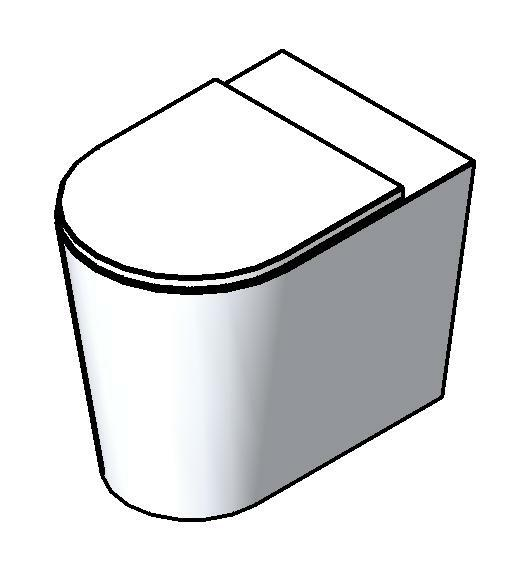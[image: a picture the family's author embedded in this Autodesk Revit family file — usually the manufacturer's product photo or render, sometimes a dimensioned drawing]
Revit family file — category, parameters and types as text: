
# Revit family: Deca_Bacia Sanitaria Convencional_LK_P.23
name_source: partatom
category: Plumbing Fixtures
units: mm (PartAtom-declared; Revit-internal decimal feet)

## family parameters
Cut with Voids When Loaded = No
Host = Face
Part Type = Normal
Room Calculation Point = No
Round Connector Dimension = Use Radius
Shared = No

## types (5) — shared parameters
Acompanha o Produto = -
Aprovado por = quattroD
Atendimento ao Cliente = 0800-0117073
Categoria = BACIAS E BIDES
Composição Anel Vedação = Não Possui
Composição Assento = -
Composição Básica = Argila, feldspato, caulim, vidrados e corantes inorgânicos.
Composição Componente = Não Possui
Consumo = 6 lpf
Cor Interna = -
Cor Secundária = -
Cores Componente = -
Criado por = quattroD
Código Pai = P.23
Description = Bacia convencional
Diâmetro Ponto de Esgoto = 0.1 m
Diâmetro Água Fria = 0.04 m
Informações Complementares = -
Itens de Instalação = 1200.C.KIT.P
Linha = LK
Manufacturer = Deca
Norma = NBR-16727-1;NBR-16727-2
Peso Líquido (Kg) = 32.341
Pressão máx. funcionamento = -
Pressão mín. Aquec. Acúmulo = -
Pressão mín. Aquec. Passagem = -
Pressão mín. funcionamento = -
Raio Ponto de Esgoto = 0.05 m
Raio Água Fria = 0.02 m
Saída de Esgoto = Saída de Esgoto Vertical
Segmento = Banheiro Luxo
Tipo de dispositivo economizador = -
Tipo de mecanismo utilizado = -
Tipo de rosca de entrada = -
Tipo de rosca de saída = -
URL = www.deca.com.br
Vazão na Pressão máx. (L/min) = -
Vazão na Pressão mín. (L/min) = -
zero-valued in all types: CWFU, Default Elevation, WFU

## per-type parameters (varying)
| type | Cor Principal | Material | Model |
| P.23.86_Cinza Fosco | Cinza Fosco | Deca_Cinza Fosco | P.23.86 |
| P.23.22_Marrom Fosco | Marrom Fosco | Deca_Marrom Fosco | P.23.22 |
| P.23.17_Branco | Branco | Deca_Branco | P.23.17 |
| P.23.94_Ébano Fosco | Ébano Fosco | Deca_Ébano Fosco | P.23.94 |
| P.23.95_Ébano | Ébano | Deca_Ébano | P.23.95 |

## geometry (parser evidence)
native form markers: Sweep x3
no freeform markers — native parametric forms only
